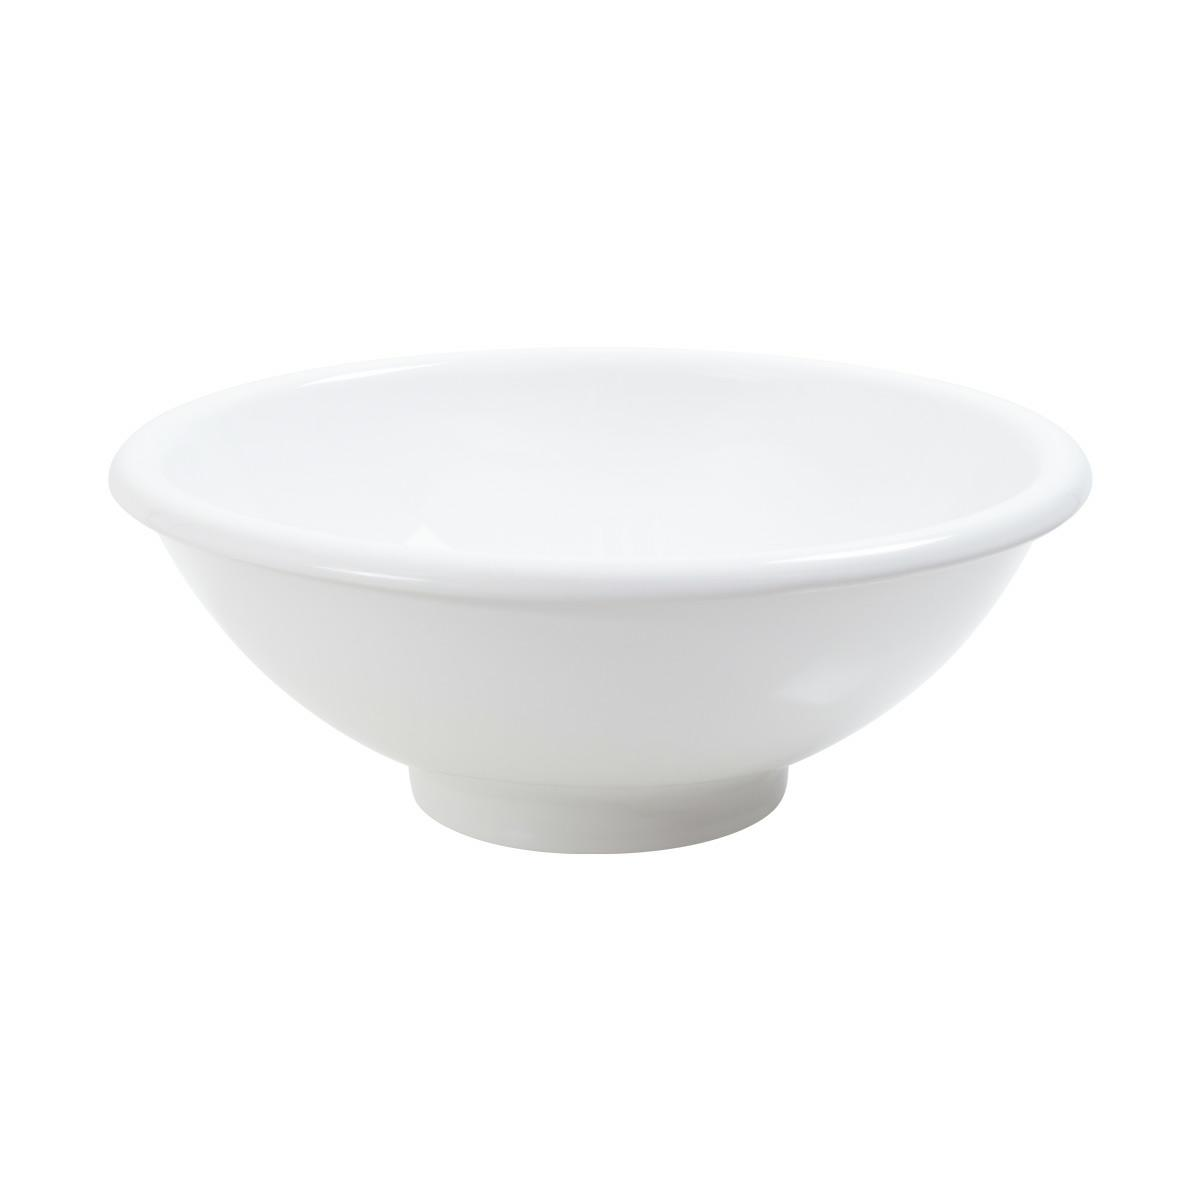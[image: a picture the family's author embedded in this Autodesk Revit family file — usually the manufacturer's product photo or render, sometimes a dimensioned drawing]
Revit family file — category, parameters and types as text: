
# Revit family: CCMX-CORONA_MANANTIAL-DUO
name_source: partatom
category: Plumbing Fixtures
units: mm (PartAtom-declared; Revit-internal decimal feet)

## family parameters
Always vertical = Yes
Cut with Voids When Loaded = No
OmniClass Number = 23.45.00.00
OmniClass Title = Sanitary, Laundry, and Cleaning Equipment
Part Type = Normal
Room Calculation Point = No
Round Connector Dimension = Use Diameter
Shared = No
Work Plane-Based = No

## types (1)
- CCMX-CORONA_MANANTIAL-DUO
    Assembly Code = D2010.60
    Description = Diseño con doble propósito para ser instalado como lavamanos tipo bowl o de sobreponer. Tiene un práctico tamaño para espacios reducidos, se recomienda instalar con griferías a la pared o de mesón.
    Dimensiones = https://coronamexico.com
    Ficha Tecnica = https://coronamexico.com
    Garantia de Producto = 20 años en porcelana sanitaria
    Keynote = 224116
    Manual de Instalacion = https://coronamexico.com
    Manufacturer = CORONA
    Model = Manantial
    Type Image = MANANTIAL.jpg
    URL = https://coronamexico.com

## geometry (parser evidence)
native form markers: Sweep x3
no freeform markers — native parametric forms only
